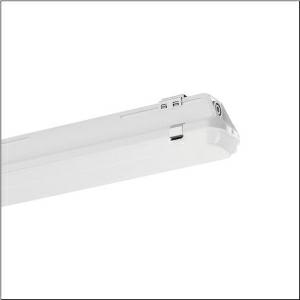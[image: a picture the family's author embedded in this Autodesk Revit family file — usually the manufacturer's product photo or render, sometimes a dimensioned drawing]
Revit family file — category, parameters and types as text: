
# Revit family: monsun_r__21_51fb10dp460c007_91e3
name_source: partatom
category: Lighting Fixtures
units: mm (PartAtom-declared; Revit-internal decimal feet)

## family parameters
Cut with Voids When Loaded = No
Host = Face
Light Source = No
Part Type = Normal
Room Calculation Point = No
Round Connector Dimension = Use Diameter
Shared = No

## types (1)
- --- (1 x LED, 6060 lm, 32.7 W, 4000K)
    Apparent Load = 33 VA
    CIE Flux Codes = 47 77 93 94 100
    Color Rendering = 80
    Color Temperature = 4000K
    Default Elevation = 1800 mm
    Description = Monsun® 21, damp-proof luminaire, chain hanger, primary optical cover: enclosure, of PMMA, light emission: direct distribution, primary light characteristic: symmetric, installation type: suspended mounting, surface-mounted, horizontal mounting, vertical mounting, LED, rated luminous flux: 6.060lm, luminous efficacy: 185lm/W, light colour: 840, colour temperature: 4000K, control gear: DALI 2, with terminal, 5-pole, max. 2.5mm², through-wiring: 7x 2.5mm², mains connection: 220..240V, AC, 50/60Hz, rated input power: 33W, housing, of glass-fibre reinforced polyester, uncoated, bright grey, incl. chain hanger, length: 1.590mm, width: 90mm, height: 88mm, clip for enclosure, of stainless steel (V2A), ceiling mounting element, of stainless steel (V2A), chain hanger, of stainless steel (V2A), protection rating (complete): IP66, insulation class (complete): insulation class I (protective earthing), certification: CE, ENEC, VDE, UKCA, protection symbol: D, impact resistance: IK04, permissible operating ambient temperature: -25..+35°C, standard: EN 50419, EN 60598-2-1, corresponds to IFS (International Featured Standards) requirements for safety and quality in the food industry, for indoor or canopied outdoor use, no direct snow, no direct sun, no direct rain, LABS conformity tested according to VDMA 24364:2018-05, contact your sales advisor before using the luminaires in applications with unclear chemical exposure, large temperature fluctuations or condensation-forming humidity, packaging unit: 1 piece
    Height = 89 mm
    Lamp = 1 x LED
    Lamp Light Flux = 6060 lm
    Lamp Power = 32.7 W
    Lamp count = 1
    Length = 1590 mm
    Luminous efficacy = 185 lm/W
    Manufacturer = Siteco
    ModVariant = No
    Model = 51FB10DP460C007
    Mounting Place = Ceiling
    Mounting Type = Surface mounted
    Number of Poles = 1
    OnlyDefault = Yes
    Power Factor = 1
    Product Name = Monsun® 21
    Product group = damp-proof luminaire
    ProductGroupID = 301
    Protection Class = Protection class I
    Protection Degree = IP 66
    RLX_Detail_Level = 1
    RLX_Emergency_Light_Flux = 0 lm
    RLX_Emergency_Type = 0
    RLX_Emergency_Type_DB = No
    RlxData = <blob elided: 92317 chars, md5=166f8ad7>
    Socket = socket
    Standby Power = 0 W
    System Light Flux = 6060 lm
    System Power = 33 W
    Type Comments = factory setting: luminous flux: 100 % | dim-lin: 254 | 229 mA
    Type Image = l_1319656.jpg
    URL = http://relux.com
    VarID = @adj_051923
    Voltage = 0 V
    Weight = 0.00 kg
    Width = 90 mm

## geometry (parser evidence)
native form markers: Blend x4, Sweep x13
no freeform markers — native parametric forms only
